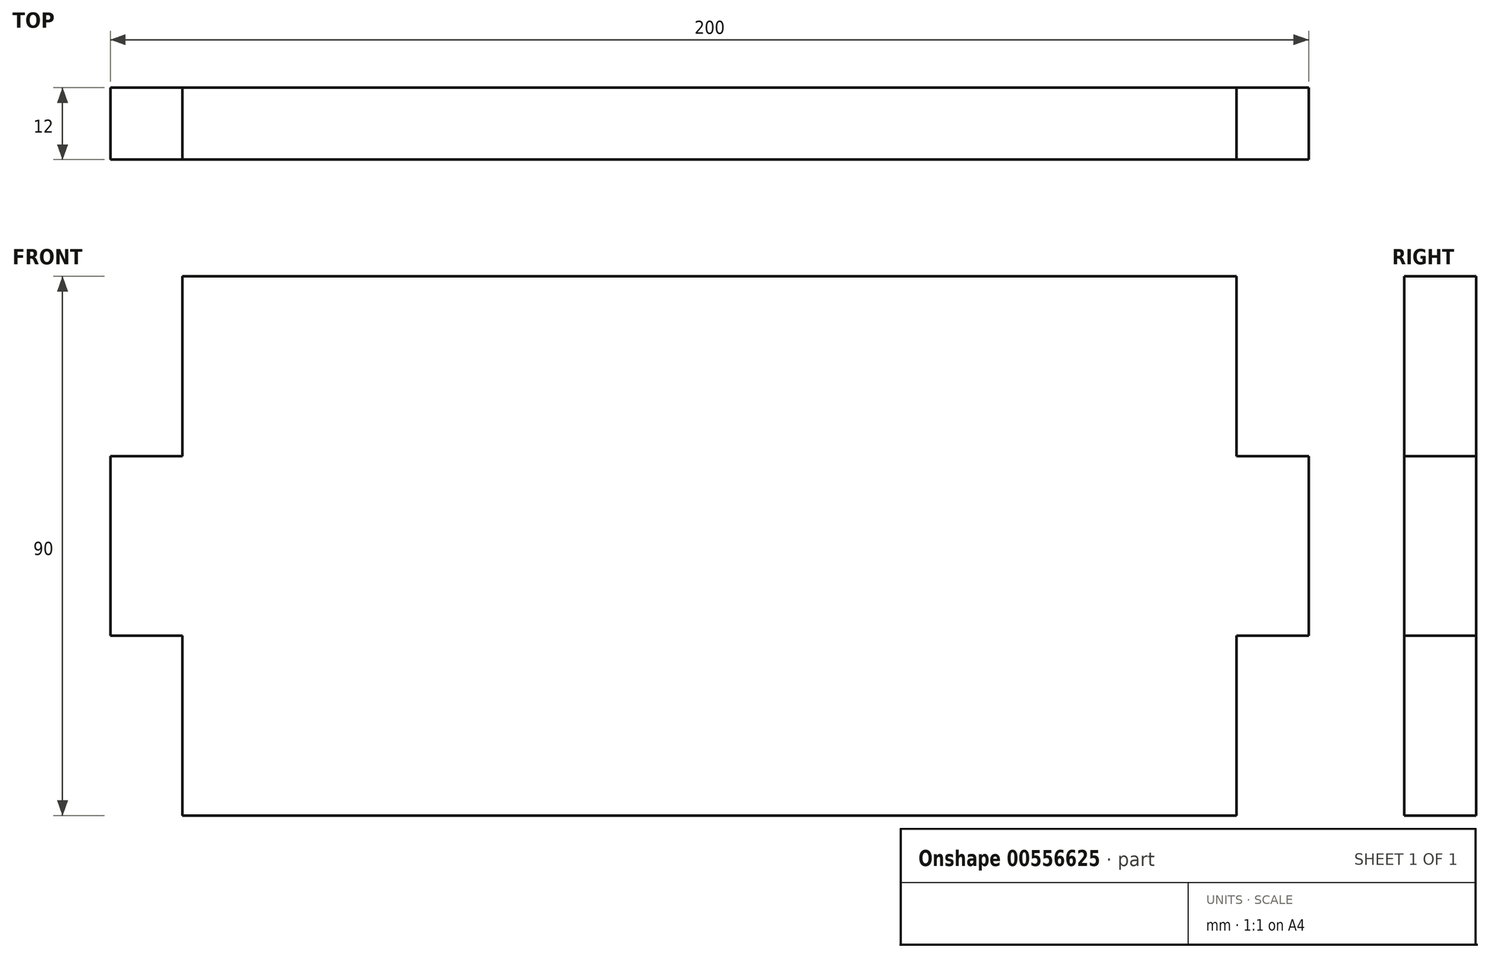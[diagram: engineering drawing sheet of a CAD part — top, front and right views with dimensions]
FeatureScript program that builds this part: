
annotation { "Feature Type Name" : "Feature", "Feature Type Description" : "" }
export const myFeature = defineFeature(function(context is Context, id is Id, definition is map)
    precondition{}
    {
        {
            var Q0;
            Q0=qCreatedBy(makeId("Front.planeOp"),FACE);
            var sketch = newSketch(context, id + "F0", { "sketchPlane" : qUnion([Q0])});
            skLineSegment(sketch, "E0", {"start": v(0, 0) * mm, "end": v(0, 30) * mm});
            skLineSegment(sketch, "E1", {"start": v(0, 30) * mm, "end": v(-12, 30) * mm});
            skLineSegment(sketch, "E2", {"start": v(-12, 30) * mm, "end": v(-12, 60) * mm});
            skLineSegment(sketch, "E3", {"start": v(-12, 60) * mm, "end": v(0, 60) * mm});
            skLineSegment(sketch, "E4", {"start": v(0, 60) * mm, "end": v(0, 90) * mm});
            skLineSegment(sketch, "E5", {"start": v(0, 90) * mm, "end": v(88, 90) * mm});
            skLineSegment(sketch, "E6", {"start": v(88, 90) * mm, "end": v(88, 0) * mm, "construction": true});
            skLineSegment(sketch, "E7", {"start": v(88, 0) * mm, "end": v(0, 0) * mm});
            skLineSegment(sketch, "E8.MirrorCS", {"start": v(88, 0) * mm, "end": v(176, 0) * mm});
            skLineSegment(sketch, "E9.MirrorCS", {"start": v(176, 0) * mm, "end": v(176, 30) * mm});
            skLineSegment(sketch, "E10.MirrorCS", {"start": v(176, 60) * mm, "end": v(176, 90) * mm});
            skLineSegment(sketch, "E11.MirrorCS", {"start": v(188, 30) * mm, "end": v(188, 60) * mm});
            skLineSegment(sketch, "E12.MirrorCS", {"start": v(176, 30) * mm, "end": v(188, 30) * mm});
            skLineSegment(sketch, "E13.MirrorCS", {"start": v(188, 60) * mm, "end": v(176, 60) * mm});
            skLineSegment(sketch, "E14.MirrorCS", {"start": v(176, 90) * mm, "end": v(88, 90) * mm});
            skSolve(sketch);
        }
        {
            var Q0;
            Q0=makeQuery(id+"F0.imprint","IMPRINT",FACE,{"disambiguationData":[TD([[makeQuery(id+"F0.imprint","IMPRINT",EDGE,{"derivedFrom":sQuery(id+"F0.wireOp",EDGE,"E0")}),-1.0]])]});
            extrude(context, id + "F1", {"entities" : qUnion([Q0]), "endBound" : BoundingType.SYMMETRIC, "depth" : 12 * mm, "offsetDistance" : 25 * mm});
        }
    });
